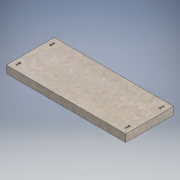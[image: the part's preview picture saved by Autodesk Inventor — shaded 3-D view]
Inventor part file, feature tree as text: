
AUTODESK INVENTOR PART (.ipt)
format: ipt  version: 2022.2 (Build 262287010, 287A)  size: 267,776 bytes
history: native  units: in
note: dims shown in document units (in); Inventor stores cm internally (conversion verified against a paired STEP export)
features: other x15, revolve x6, sketch x4, extrude x1, projected_geometry x1
ambient origin geometry x8: Origin, YZ Plane, XZ Plane, XY Plane, X Axis, Y Axis, Z Axis, Center Point
bodies: Solid1 (feature_tree)
feature tree (27):
  other  "B soffit"
  other  "Blocks"
  extrude  "Extrusion1"  Depth=19.0in
  sketch  "Sketch2"  dims[d2=47.375in d3=0.0in d4=2.0in]
  revolve  "Revolution1"  [1 undecoded]
  revolve  "Revolution2"  Angle=90.0deg
  sketch  "Sketch3"  dims[d5=1.0in d6=90.0deg]
  revolve  "Revolution3"  Angle=90.0deg
  revolve  "Revolution4"  Angle=90.0deg
  sketch  "Sketch4"  dims[d7=90.0deg d8=90.0deg d9=90.0deg d10=90.0deg d11=90.0deg]
  revolve  "Revolution5"  Angle=90.0deg
  revolve  "Revolution6"  Angle=90.0deg
  sketch  "Sketch1"  dims[d0=2.0in d1=19.0in]
  other  "Bolt"
  other  "Block2"
  other  "Block3"
  projected_geometry  "Projected Loop1"
  other  "Bolt:1"
  other  "Block2:1"
  other  "Block2:2"
  other  "Block2:3"
  other  "Block3:1"
  other  "Block3:2"
  other  "Block3:3"
  other  "Block3:4"
  other  "Block3:5"
  other  "Block3:6"
note: 1 required parameter value undecoded (feature->parameter linkage not recoverable at this tier; creation-order binding heuristic only, values carry confidence <= 0.55)
